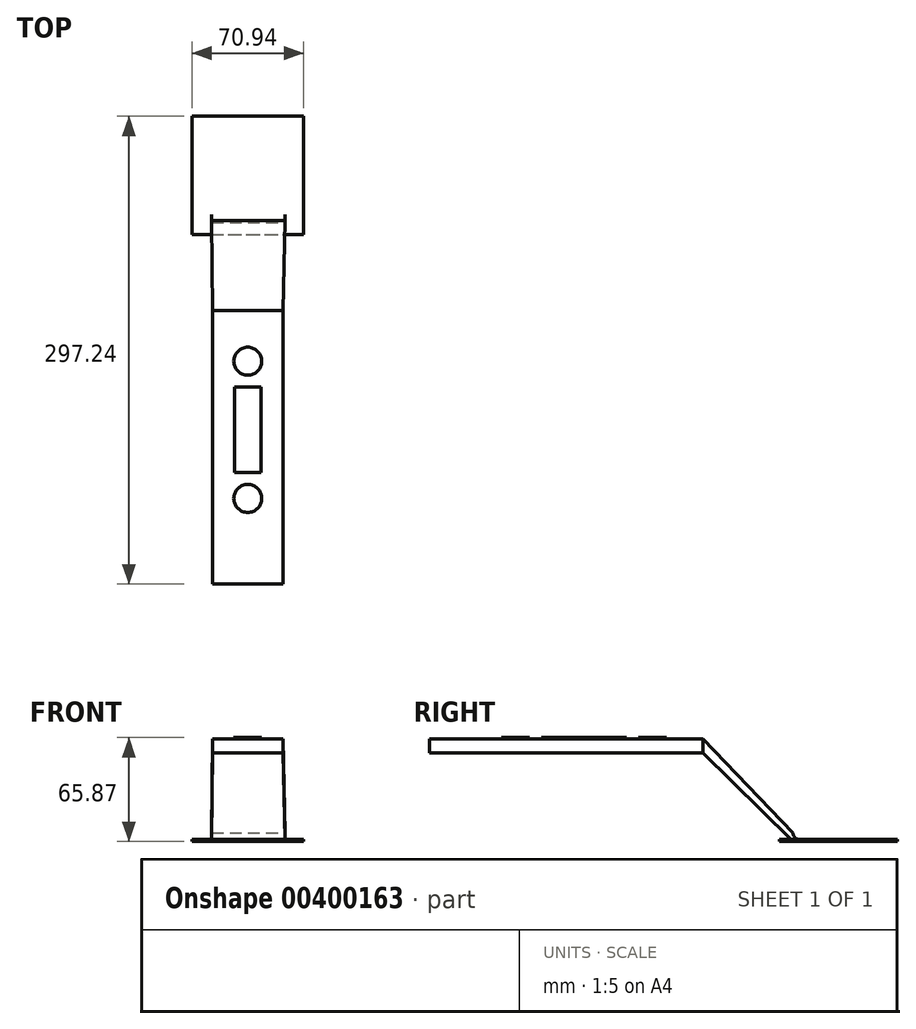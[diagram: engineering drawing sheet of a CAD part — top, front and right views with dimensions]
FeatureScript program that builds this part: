
annotation { "Feature Type Name" : "Feature", "Feature Type Description" : "" }
export const myFeature = defineFeature(function(context is Context, id is Id, definition is map)
    precondition{}
    {
        {
            var Q0;
            Q0=qCreatedBy(makeId("Top.planeOp"),FACE);
            var sketch = newSketch(context, id + "F0", { "sketchPlane" : qUnion([Q0])});
            skLineSegment(sketch, "E0.bottom", {"start": v(-35.47, 66.35) * mm, "end": v(35.47, 66.35) * mm});
            skLineSegment(sketch, "E0.top", {"start": v(-35.47, -8.76) * mm, "end": v(35.47, -8.76) * mm});
            skLineSegment(sketch, "E0.left", {"start": v(-35.47, 66.35) * mm, "end": v(-35.47, -8.76) * mm});
            skLineSegment(sketch, "E0.right", {"start": v(35.47, 66.35) * mm, "end": v(35.47, -8.76) * mm});
            skPoint(sketch, "E0.middle", {"position": v(0, 28.8) * mm});
            skSolve(sketch);
        }
        {
            var Q0;
            Q0=makeQuery(id+"F0.imprint","IMPRINT",FACE,{"disambiguationData":[TD([[makeQuery(id+"F0.imprint","IMPRINT",EDGE,{"derivedFrom":sQuery(id+"F0.wireOp",EDGE,"E0.bottom")}),-1.0]])]});
            extrude(context, id + "F1", {"entities" : qUnion([Q0]), "depth" : 1.27 * mm});
        }
        {
            var Q0;
            Q0=qCreatedBy(makeId("Front.planeOp"),FACE);
            cPlane(context, id + "F2", {"entities" : qUnion([Q0]), "cplaneType" : CPlaneType.OFFSET, "offset" : 57.15 * mm, "width" : 152.4 * mm, "height" : 152.4 * mm});
        }
        {
            var Q0;
            Q0=qCreatedBy(makeId("Front.planeOp"),FACE);
            var sketch = newSketch(context, id + "F3", { "sketchPlane" : qUnion([Q0])});
            skLineSegment(sketch, "E1.bottom", {"start": v(-22.88, 5.28) * mm, "end": v(23.76, 5.28) * mm});
            skLineSegment(sketch, "E1.top", {"start": v(-22.88, 0) * mm, "end": v(23.76, 0) * mm});
            skLineSegment(sketch, "E1.left", {"start": v(-22.88, 5.28) * mm, "end": v(-22.88, 0) * mm});
            skLineSegment(sketch, "E1.right", {"start": v(23.76, 5.28) * mm, "end": v(23.76, 0) * mm});
            skSolve(sketch);
        }
        {
            var Q0;
            Q0=qCreatedBy(id+"F2.planeOp",FACE);
            var sketch = newSketch(context, id + "F4", { "sketchPlane" : qUnion([Q0])});
            skLineSegment(sketch, "E2.bottom", {"start": v(-22.44, 56.3) * mm, "end": v(22.44, 56.3) * mm});
            skLineSegment(sketch, "E2.top", {"start": v(-22.44, 65.1) * mm, "end": v(22.44, 65.1) * mm});
            skLineSegment(sketch, "E2.left", {"start": v(-22.44, 56.3) * mm, "end": v(-22.44, 65.1) * mm});
            skLineSegment(sketch, "E2.right", {"start": v(22.44, 56.3) * mm, "end": v(22.44, 65.1) * mm});
            skPoint(sketch, "E2.middle", {"position": v(0, 60.7) * mm});
            skSolve(sketch);
        }
        {
            var Q1;
            Q1=makeQuery(id+"F3.imprint","IMPRINT",FACE,{"disambiguationData":[TD([[makeQuery(id+"F3.imprint","IMPRINT",EDGE,{"derivedFrom":sQuery(id+"F3.wireOp",EDGE,"E1.bottom")}),-1.0]])]});
            var Q2;
            Q2=makeQuery(id+"F4.imprint","IMPRINT",FACE,{"disambiguationData":[TD([[makeQuery(id+"F4.imprint","IMPRINT",EDGE,{"derivedFrom":sQuery(id+"F4.wireOp",EDGE,"E2.bottom")}),1.0]])]});
            loft(context, id + "F5", {"operationType" : NewBodyOperationType.ADD, "sheetProfilesArray" : [{ "sheetProfileEntities" : qUnion([Q1]) }, { "sheetProfileEntities" : qUnion([Q2]) }]});
        }
        {
            var Q0;
            Q0=makeQuery(id+"F5.boolean.opBoolean","INTERSECT",EDGE,{"derivedFrom":[makeQuery(id+"F1.opExtrude","CAP_FACE",FACE,{"disambiguationData":[OSD([sQuery(id+"F0.wireOp",EDGE,"E0.bottom"),sQuery(id+"F0.wireOp",EDGE,"E0.top"),sQuery(id+"F0.wireOp",EDGE,"E0.left"),sQuery(id+"F0.wireOp",EDGE,"E0.right")])],"isStart":false}),makeQuery(id+"F5.opLoft","CAP_FACE",FACE,{"disambiguationData":[OSD([makeQuery(id+"F3.imprint","IMPRINT",FACE,{"disambiguationData":[TD([[makeQuery(id+"F3.imprint","IMPRINT",EDGE,{"derivedFrom":sQuery(id+"F3.wireOp",EDGE,"E1.bottom")}),-1.0]])]})])],"isStart":true})]});
            fillet(context, id + "F6", {"entities" : qUnion([Q0]), "radius" : 3.8 * mm, "tangentPropagation" : true, "allowEdgeOverflow" : false});
        }
        {
            var Q0;
            Q0=makeQuery(id+"F5.opLoft","CAP_FACE",FACE,{"disambiguationData":[OSD([makeQuery(id+"F4.imprint","IMPRINT",FACE,{"disambiguationData":[TD([[makeQuery(id+"F4.imprint","IMPRINT",EDGE,{"derivedFrom":sQuery(id+"F4.wireOp",EDGE,"E2.bottom")}),1.0]])]})])],"isStart":true});
            var sketch = newSketch(context, id + "F7", { "sketchPlane" : qUnion([Q0])});
            skSolve(sketch);
        }
        {
            var Q0;
            Q0 = qSketchRegion(id + "F7", true);
            var Q1;
            {var subQ0=sQuery(id+"F4.wireOp",EDGE,"E2.right");var subQ1=sQuery(id+"F4.wireOp",EDGE,"E2.left");var subQ2=sQuery(id+"F4.wireOp",EDGE,"E2.bottom");Q1=makeQuery(id+"F7.imprint","IMPRINT",FACE,{"disambiguationData":[TD([[makeQuery(id+"F7.imprint","IMPRINT",EDGE,{"derivedFrom":makeQuery(id+"F5.opLoft","MID_CAP_EDGE",EDGE,{"disambiguationData":[OSD([subQ2,subQ1,subQ0])],"capPos":1.0})}),1.0]])]});}
            extrude(context, id + "F8", {"entities" : qUnion([Q0, Q1]), "operationType" : NewBodyOperationType.ADD, "depth" : 173.74 * mm});
        }
        {
            var Q0;
            Q0=makeQuery(id+"F8.opExtrude","SWEPT_FACE",FACE,{"disambiguationData":[OSD([sQuery(id+"F4.wireOp",EDGE,"E2.top"),sQuery(id+"F4.wireOp",EDGE,"E2.left"),sQuery(id+"F4.wireOp",EDGE,"E2.right")])]});
            var sketch = newSketch(context, id + "F9", { "sketchPlane" : qUnion([Q0])});
            skLineSegment(sketch, "E3.bottom", {"start": v(-8.53, -159.94) * mm, "end": v(8.53, -159.94) * mm});
            skLineSegment(sketch, "E3.top", {"start": v(-8.53, -105.8) * mm, "end": v(8.53, -105.8) * mm});
            skLineSegment(sketch, "E3.left", {"start": v(-8.53, -159.94) * mm, "end": v(-8.53, -105.8) * mm});
            skLineSegment(sketch, "E3.right", {"start": v(8.53, -159.94) * mm, "end": v(8.53, -105.8) * mm});
            skPoint(sketch, "E3.middle", {"position": v(0, -132.87) * mm});
            skSolve(sketch);
        }
        {
            var Q0;
            Q0=makeQuery(id+"F9.imprint","IMPRINT",FACE,{"disambiguationData":[TD([[makeQuery(id+"F9.imprint","IMPRINT",EDGE,{"derivedFrom":sQuery(id+"F9.wireOp",EDGE,"E3.bottom")}),1.0]])]});
            extrude(context, id + "F10", {"entities" : qUnion([Q0]), "operationType" : NewBodyOperationType.ADD, "depth" : 0.76 * mm});
        }
        {
            var Q0;
            Q0=makeQuery(id+"F8.opExtrude","SWEPT_FACE",FACE,{"disambiguationData":[OSD([sQuery(id+"F4.wireOp",EDGE,"E2.top"),sQuery(id+"F4.wireOp",EDGE,"E2.left"),sQuery(id+"F4.wireOp",EDGE,"E2.right")])]});
            var sketch = newSketch(context, id + "F11", { "sketchPlane" : qUnion([Q0])});
            skCircle(sketch, "E4", {"center": v(0, -89.28) * mm, "radius": 8.9 * mm});
            skSolve(sketch);
        }
        {
            var Q0;
            Q0=makeQuery(id+"F11.imprint","IMPRINT",FACE,{"disambiguationData":[TD([[makeQuery(id+"F11.imprint","IMPRINT",EDGE,{"derivedFrom":sQuery(id+"F11.wireOp",EDGE,"E4")}),-1.0]])]});
            var sketch = newSketch(context, id + "F12", { "sketchPlane" : qUnion([Q0])});
            skCircle(sketch, "E5", {"center": v(0, -176.45) * mm, "radius": 8.9 * mm});
            skSolve(sketch);
        }
        {
            var Q0;
            Q0=makeQuery(id+"F12.imprint","IMPRINT",FACE,{"disambiguationData":[TD([[makeQuery(id+"F12.imprint","IMPRINT",EDGE,{"derivedFrom":sQuery(id+"F12.wireOp",EDGE,"E5")}),1.0]])]});
            extrude(context, id + "F13", {"entities" : qUnion([Q0]), "operationType" : NewBodyOperationType.ADD, "depth" : 0.76 * mm});
        }
        {
            var Q0;
            Q0=makeQuery(id+"F11.imprint","IMPRINT",FACE,{"disambiguationData":[TD([[makeQuery(id+"F11.imprint","IMPRINT",EDGE,{"derivedFrom":sQuery(id+"F11.wireOp",EDGE,"E4")}),1.0]])]});
            extrude(context, id + "F14", {"entities" : qUnion([Q0]), "operationType" : NewBodyOperationType.ADD, "depth" : 0.76 * mm});
        }
    });
